# Revit family: P300331-134-30
name_source: partatom
category: Lighting Fixtures
units: mm (PartAtom-declared; Revit-internal decimal feet)

## family parameters
Cut with Voids When Loaded = No
Host = Face
Light Source = Yes
OmniClass Number = 23.80.70.11.14.17
OmniClass Title = Direct/Indirect
Part Type = Normal
Room Calculation Point = No
Round Connector Dimension = Use Diameter
Shared = Yes

## types (1)
- P300331-134-30
    Apparent Load = 14 VA
    Assembly Code = D5020200
    Color Filter = 16777215
    Connector Description = Lighting Connector
    Default Elevation = 48 "
    Description = Grid LED Collection 14-inch Silver Ridge and White Linen Acrylic Modern Style Bath Vanity Wall Light
    Dimming Lamp Color Temperature Shift = <None>
    Features = Blend a dramatic look and soft illumination, with the Grid LED Collection 14-Inch 1-Light Silver Ridge White Linen LED Modern Linear Bath Vanity Light ideal for any entryway, hallway, foyer, bedroom, sitting room, living room, or bathroom.
Styles: Perfect for contemporary and modern style settings.
Finish: The geometric, open-cage frame is coated in a silver ridge finish.
Materials: Constructed from steel to ensure a long product lifespan. Mount the light fixture vertically or horizontally.
Glass/Shade: A light source glows from inside a cylindrical acrylic white etched linen diffuser for soft illumination.
Bulbs: For ideal illumination, 1 integrated LED module is included (14w)
3000k
90CRI
569 delivered lumens
dimmable
Dimensions: Measures 14-inch width by 4-3/4-inch height by 3-1/8-inch depth
Certifications: cETLus damp location listed
Energy Star qualified
meets California Title 24 JA8-2019
Pairs With: Pairs with a variety of Progress Lighting fixtures.
Warranty: Our 5-Year Limited Warranty guarantees your complete satisfaction with your purchase and includes professional after-sales customer service support.
    Fixture distribution = Direct
    Glass = Hubbell - White Glass
    Housing Material = Paint - Hubbell - Metallic Silver Textured
    Lamp = LED
    Load Classification = Lighting
    Manufacturer = Progress Lighting
    Model = P300331-134-30
    Photometric Web File = generic.ies
    Power Factor = 1
    Product Documentation Link = https://hubbellcdn.com
    Product Link = https://www.hubbell.com
    Tilt Angle = -180.00°
    URL = https://www.hubbell.com
    Voltage = 120 V
    Warranty = 5 years Warranty
    Wattage Comments = 14W
    Watts = 14 W

## geometry (parser evidence)
native form markers: Blend x4, Sweep x4
no freeform markers — native parametric forms only
